# Revit family: OV-T 縦手摺b
name_source: partatom
category: 手すり
revit_build: Autodesk Revit 2018 (Build: 20170223_1515(x64)
units: mm (PartAtom-declared; Revit-internal decimal feet)

## family parameters
ホスト = 壁
ロード時にボイドで切り取り = いいえ
共有 = いいえ
常に垂直 = はい

## types (6) — shared parameters
タイプの説明 = 楕円手摺40×32
笠木通路側 = 笠木No.10プレーンホワイト
製造元 = ナカ工業株式会社
説明 = 便所多用途　GB-R-H以上の壁面強度
高強度壁用 = はい

## per-type parameters (varying)
| type | 座金下位置 | 手摺L | 笠木壁側 | 笠木長 |
| OV-T800H ツートンカラー | 468 | 800  [stored 2.62467 ft] | 笠木No.04ソフトブラック | 812 |
| OV-T600H ツートンカラー | 668 | 600 | 笠木No.04ソフトブラック | 612 |
| OV-T400H ツートンカラー | 868 | 400  [stored 1.31234 ft] | 笠木No.04ソフトブラック | 412 |
| OV-T400H 10プレーンホワイト | 868 | 400  [stored 1.31234 ft] | 笠木No.10プレーンホワイト | 412 |
| OV-T600H 10プレーンホワイト | 668 | 600 | 笠木No.10プレーンホワイト | 612 |
| OV-T800H 10プレーンホワイト | 468 | 800  [stored 2.62467 ft] | 笠木No.10プレーンホワイト | 812 |

note: [stored X ft] marks values corroborated as IEEE doubles in the binary element streams (Revit-internal decimal feet)

## geometry (parser evidence)
native form markers: Blend x2
no freeform markers — native parametric forms only
